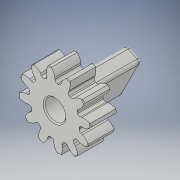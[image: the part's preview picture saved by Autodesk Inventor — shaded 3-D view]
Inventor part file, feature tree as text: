
AUTODESK INVENTOR PART (.ipt)
format: ipt  version: 2019 (Build 230136000, 136)  size: 483,840 bytes
history: native  units: mm
features: extrude x3, sketch x3, fillet x2, projected_geometry x1, chamfer x1
ambient origin geometry x8: Origin, YZ Plane, XZ Plane, XY Plane, X Axis, Y Axis, Z Axis, Center Point
bodies: Solid1 (feature_tree)
feature tree (10):
  extrude  "Extrusion1"  Depth=4.0mm
  extrude  "Extrusion2"  Depth=1.0mm TaperAngle=0.0deg
  extrude  "Extrusion3"  Depth=7.0mm
  fillet  "Fillet1"  Radius=7.0mm
  fillet  "Fillet2"  Radius=0.5mm
  sketch  "Sketch1"  dims[d0=20.0mm d1=4.0mm]
  projected_geometry  "Projected Loop1"
  sketch  "Sketch2"  dims[d2=25.4mm d3=0.0mm d4=1.0mm d5=0.0mm]
  sketch  "Sketch3"  dims[d6=2.5mm d7=7.0mm d8=7.0mm d9=0.0mm d10=0.5mm d11=0.5mm]
  chamfer  "Chamfer1"  Distance=0.5mm
